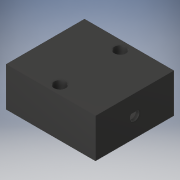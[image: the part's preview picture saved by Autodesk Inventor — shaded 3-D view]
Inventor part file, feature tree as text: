
AUTODESK INVENTOR PART (.ipt)
format: ipt  version: 2018 (Build 220112000, 112)  size: 124,416 bytes
history: native  units: in
note: dims shown in document units (in); Inventor stores cm internally (conversion verified against a paired STEP export)
features: sketch x4, extrude x3, hole x1
ambient origin geometry x8: Origin, YZ Plane, XZ Plane, XY Plane, X Axis, Y Axis, Z Axis, Center Point
bodies: Solid1 (feature_tree)
feature tree (8):
  extrude  "Extrusion1"  Depth=1.0in
  hole  "Hole1"  [1 undecoded]
  extrude  "Extrusion3"  Depth=1.1in
  extrude  "Extrusion5"  Depth=1.1in
  sketch  "Sketch1"  dims[d0=1.14in d1=1.0in]
  sketch  "Sketch2"  dims[d2=0.5in d3=0.0in d4=0.385in]
  sketch  "Sketch3"  dims[d5=0.77in]
  sketch  "Sketch5"  dims[d6=0.15in d7=0.75in d8=0.279in d9=0.093in d10=0.5635in d11=1.0in d12=0.8108in d13=0.1181in d14=0.25in d15=0.5in d18=0.0394in d19=0.3819in d20=0.0in d23=0.48in d24=0.4in d25=0.05in d26=0.05in d27=1.1in d28=0.0in]
note: 1 required parameter value undecoded (feature->parameter linkage not recoverable at this tier; creation-order binding heuristic only, values carry confidence <= 0.55)
